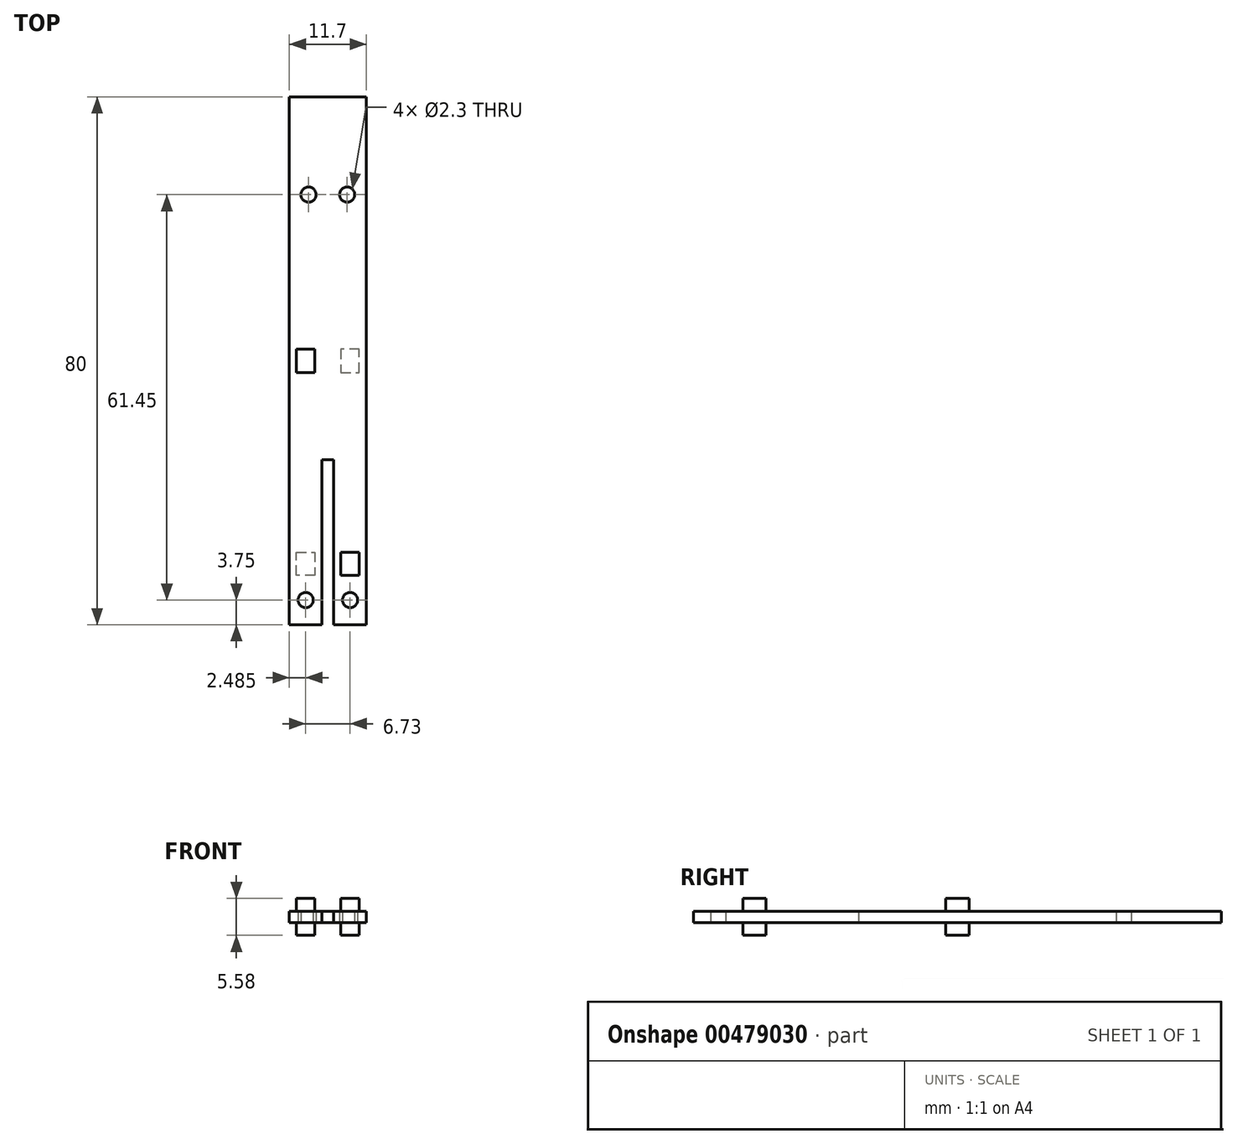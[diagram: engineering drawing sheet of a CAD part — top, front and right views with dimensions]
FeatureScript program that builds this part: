
annotation { "Feature Type Name" : "Feature", "Feature Type Description" : "" }
export const myFeature = defineFeature(function(context is Context, id is Id, definition is map)
    precondition{}
    {
        {
            var Q0;
            Q0=qCreatedBy(makeId("Top.planeOp"),FACE);
            var sketch = newSketch(context, id + "F0", { "sketchPlane" : qUnion([Q0])});
            skLineSegment(sketch, "E0", {"start": v(-5.85, 40) * mm, "end": v(-5.85, 0) * mm});
            skLineSegment(sketch, "E1", {"start": v(-5.85, 40) * mm, "end": v(5.85, 40) * mm});
            skLineSegment(sketch, "E2", {"start": v(5.85, 40) * mm, "end": v(5.85, 0) * mm});
            skLineSegment(sketch, "E3", {"start": v(-5.85, 0) * mm, "end": v(-5.85, -40) * mm});
            skLineSegment(sketch, "E4", {"start": v(-5.85, -40) * mm, "end": v(-0.88, -40) * mm});
            skLineSegment(sketch, "E5", {"start": v(-0.88, -40) * mm, "end": v(-0.88, -15) * mm});
            skLineSegment(sketch, "E6", {"start": v(5.85, 0) * mm, "end": v(5.85, -40) * mm});
            skLineSegment(sketch, "E7", {"start": v(5.85, -40) * mm, "end": v(0.88, -40) * mm});
            skLineSegment(sketch, "E8", {"start": v(0.88, -40) * mm, "end": v(0.88, -15) * mm});
            skLineSegment(sketch, "E9", {"start": v(0.88, -15) * mm, "end": v(-0.88, -15) * mm});
            skCircle(sketch, "E10", {"center": v(3.37, -36.25) * mm, "radius": 1.15 * mm});
            skCircle(sketch, "E11", {"center": v(-3.36, -36.25) * mm, "radius": 1.15 * mm});
            skCircle(sketch, "E12", {"center": v(-2.93, 25.2) * mm, "radius": 1.15 * mm});
            skCircle(sketch, "E13", {"center": v(2.92, 25.2) * mm, "radius": 1.15 * mm});
            skSolve(sketch);
        }
        {
            var Q0;
            Q0=makeQuery(id+"F0.imprint","IMPRINT",FACE,{"disambiguationData":[TD([[makeQuery(id+"F0.imprint","IMPRINT",EDGE,{"derivedFrom":sQuery(id+"F0.wireOp",EDGE,"E0")}),1.0]])]});
            extrude(context, id + "F1", {"entities" : qUnion([Q0]), "depth" : .88 * mm});
        }
        {
            var Q0;
            Q0 = qSketchRegion(id + "F0", true);
            extrude(context, id + "F2", {"entities" : qUnion([Q0]), "operationType" : NewBodyOperationType.ADD, "oppositeDirection" : true, "depth" : .88 * mm});
        }
        {
            var Q0;
            Q0=qCreatedBy(makeId("Top.planeOp"),FACE);
            var sketch = newSketch(context, id + "F3", { "sketchPlane" : qUnion([Q0])});
            skLineSegment(sketch, "E14", {"start": v(1.97, -32.5) * mm, "end": v(1.97, -29) * mm});
            skLineSegment(sketch, "E15", {"start": v(1.97, -29) * mm, "end": v(4.76, -29) * mm});
            skLineSegment(sketch, "E16", {"start": v(4.76, -29) * mm, "end": v(4.76, -32.5) * mm});
            skLineSegment(sketch, "E17", {"start": v(4.76, -32.5) * mm, "end": v(1.97, -32.5) * mm});
            skPoint(sketch, "E18.centerSnap0", {"position": v(3.37, -32.5) * mm});
            skSolve(sketch);
        }
        {
            var Q0;
            Q0 = qSketchRegion(id + "F3", true);
            extrude(context, id + "F4", {"entities" : qUnion([Q0]), "operationType" : NewBodyOperationType.ADD, "depth" : 2.8 * mm});
        }
        {
            var Q0;
            Q0=qCreatedBy(makeId("Top.planeOp"),FACE);
            var sketch = newSketch(context, id + "F5", { "sketchPlane" : qUnion([Q0])});
            skLineSegment(sketch, "E19", {"start": v(-1.96, -32.5) * mm, "end": v(-4.76, -32.5) * mm});
            skLineSegment(sketch, "E20", {"start": v(-4.76, -32.5) * mm, "end": v(-4.76, -29) * mm});
            skLineSegment(sketch, "E21", {"start": v(-4.76, -29) * mm, "end": v(-1.96, -29) * mm});
            skLineSegment(sketch, "E22", {"start": v(-1.96, -29) * mm, "end": v(-1.96, -32.5) * mm});
            skSolve(sketch);
        }
        {
            var Q0;
            Q0 = qSketchRegion(id + "F5", true);
            extrude(context, id + "F6", {"entities" : qUnion([Q0]), "operationType" : NewBodyOperationType.ADD, "oppositeDirection" : true, "depth" : 2.8 * mm});
        }
        {
            var Q0;
            Q0=qCreatedBy(makeId("Top.planeOp"),FACE);
            var sketch = newSketch(context, id + "F7", { "sketchPlane" : qUnion([Q0])});
            skLineSegment(sketch, "E23", {"start": v(-1.97, 0) * mm, "end": v(-1.97, -1.75) * mm});
            skLineSegment(sketch, "E24", {"start": v(-4.77, -1.75) * mm, "end": v(-4.77, 0) * mm});
            skLineSegment(sketch, "E25", {"start": v(-4.77, -1.75) * mm, "end": v(-1.97, -1.75) * mm});
            skLineSegment(sketch, "E26", {"start": v(-4.77, 0) * mm, "end": v(-4.77, 1.75) * mm});
            skLineSegment(sketch, "E27", {"start": v(-4.77, 1.75) * mm, "end": v(-1.97, 1.75) * mm});
            skLineSegment(sketch, "E28", {"start": v(-1.97, 1.75) * mm, "end": v(-1.97, 0) * mm});
            skSolve(sketch);
        }
        {
            var Q0;
            Q0 = qSketchRegion(id + "F7", true);
            extrude(context, id + "F8", {"entities" : qUnion([Q0]), "operationType" : NewBodyOperationType.ADD, "depth" : 2.8 * mm});
        }
        {
            var Q0;
            Q0=qCreatedBy(makeId("Top.planeOp"),FACE);
            var sketch = newSketch(context, id + "F9", { "sketchPlane" : qUnion([Q0])});
            skLineSegment(sketch, "E29", {"start": v(4.76, -1.75) * mm, "end": v(4.76, 0) * mm});
            skLineSegment(sketch, "E30", {"start": v(4.76, 0) * mm, "end": v(4.76, 1.75) * mm});
            skLineSegment(sketch, "E31", {"start": v(4.76, 1.75) * mm, "end": v(1.96, 1.75) * mm});
            skLineSegment(sketch, "E32", {"start": v(1.96, 1.75) * mm, "end": v(1.96, 0) * mm});
            skLineSegment(sketch, "E33", {"start": v(1.96, 0) * mm, "end": v(1.96, -1.75) * mm});
            skLineSegment(sketch, "E34", {"start": v(1.96, -1.75) * mm, "end": v(4.76, -1.75) * mm});
            skSolve(sketch);
        }
        {
            var Q0;
            Q0 = qSketchRegion(id + "F9", true);
            extrude(context, id + "F10", {"entities" : qUnion([Q0]), "operationType" : NewBodyOperationType.ADD, "oppositeDirection" : true, "depth" : 2.8 * mm});
        }
    });
